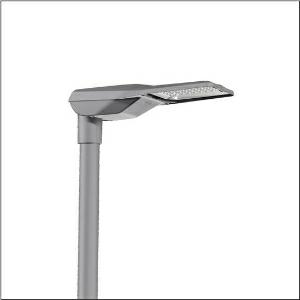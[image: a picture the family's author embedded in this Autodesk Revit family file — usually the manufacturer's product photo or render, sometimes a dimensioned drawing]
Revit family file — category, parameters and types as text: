
# Revit family: streetlight_sl_21_iq_mini___p0_8ab_5xe2r31g08hb_d767
name_source: partatom
category: Lighting Fixtures
units: mm (PartAtom-declared; Revit-internal decimal feet)

## family parameters
Cut with Voids When Loaded = No
Host = Face
Light Source = No
Part Type = Normal
Room Calculation Point = No
Round Connector Dimension = Use Diameter
Shared = No

## types (1)
- --- (1 x LED, 8210 lm, 70.9 W, 3000K)
    Apparent Load = 71 VA
    CIE Flux Codes = 36 71 98 100 100
    Color Rendering = 70
    Color Temperature = 3000K
    Default Elevation = 1800 mm
    Description = Streetlight SL 21 iQ mini, mast luminaire, primary light control with lens, of PMMA, primary optical cover: cover, of toughened safety glass, transparent, light distribution: P0.8aB, light emission: direct distribution, primary light characteristic: asymmetric, installation type: post-top, side-entry, LED, High Power LED, rated luminous flux: 8.210lm, luminous efficacy: 116lm/W, light colour: 730, colour temperature: 3000K, control gear: iQ Street-Remote, control: pre-setting: linear dimming characteristic, Street-Remote, Auto-Match, Temp-Guard, Lumen-Switch, Night-Set, Smart-Wire, Light-Fading, Desk-Remote (wireless, voltage-free reading and setting of iQ features in the workshop via application-optimized NFC function/RFID function), optimised constant luminous flux control (CLO 2.0), mains connection: 220..240V, AC, 50/60Hz, start of lifetime: 71W, end of service life: 75W, reduction: 31W, luminaire housing, of diecast aluminium, powder-coated, Siteco® metallic grey (DB 702S), corrosivity category C5 mid according to DIN EN ISO 12944, please order mast flange separately, inclination adjustable: 0°, 5°, 10°, 15°, sealing non-destructively replaceable, multi-level sealing system, length: 628mm, width: 235mm, height: 110mm, mast flange for spigot size: 42mm (side-entry): 5XC10008XM4, 60/48mm (side-entry/post-top): 5XC10108XM2, 76/60mm (side-entry/post-top): 5XC10108XM1, mounting height: 4..8m, protection rating (complete): IP66, insulation class (complete): insulation class II (safety insulation), certification: CE, ENEC, ENEC+, VDE, impact resistance: IK10, permissible operating ambient temperature for outdoor applications: -40..+50°C, standard-compliant lighting for roads and squares, packaging unit: 1 piece

Light Distribution: P0.8aB
    Height = 110 mm
    Lamp = 1 x LED
    Lamp Light Flux = 8210 lm
    Lamp Power = 70.9 W
    Lamp count = 1
    Length = 625 mm
    Luminous efficacy = 116 lm/W
    Manufacturer = Siteco
    ModVariant = No
    Model = 5XE2R31G08HB
    Number of Poles = 1
    OnlyDefault = Yes
    Power Factor = 1
    Product Name = Streetlight SL 21 iQ mini | P0.8aB
    Product group = mast luminaire | pylon top
    ProductGroupID = 6100
    Protection Class = Protection class II
    Protection Degree = IP 66
    RLX_Detail_Level = 1
    RLX_Emergency_Light_Flux = 0 lm
    RLX_Emergency_Type = 0
    RLX_Emergency_Type_DB = No
    RlxData = <blob elided: 92153 chars, md5=23f51568>
    Socket = socket
    Standby Power = 0 W
    System Light Flux = 8210 lm
    System Power = 71 W
    Type Comments = factory setting: luminous flux: 100 % | dim-lin: 254 | 711 mA
    Type Image = l_1003519.jpg
    URL = http://relux.com
    VarID = @adj_095969
    Voltage = 0 V
    Weight = 0.00 kg
    Width = 234 mm

## geometry (parser evidence)
native form markers: Blend x4, Sweep x11
no freeform markers — native parametric forms only
